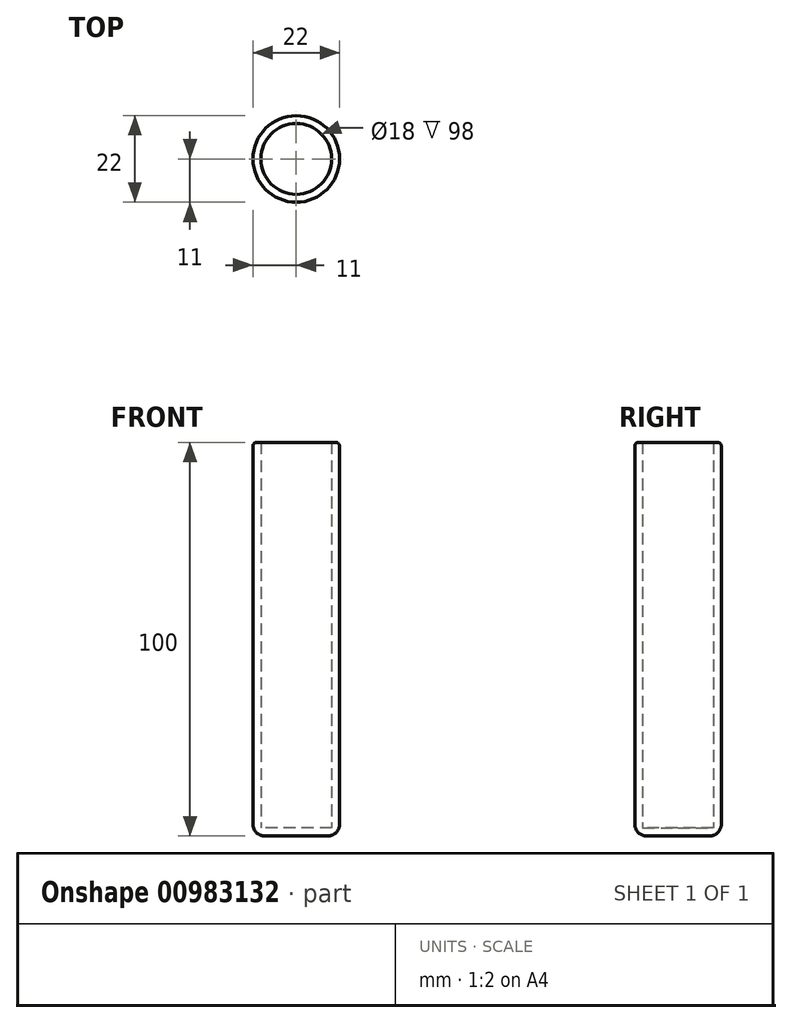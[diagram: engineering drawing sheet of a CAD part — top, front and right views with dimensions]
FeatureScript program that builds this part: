
annotation { "Feature Type Name" : "Feature", "Feature Type Description" : "" }
export const myFeature = defineFeature(function(context is Context, id is Id, definition is map)
    precondition{}
    {
        {
            var Q0;
            Q0=qCreatedBy(makeId("Top.planeOp"),FACE);
            var sketch = newSketch(context, id + "F0", { "sketchPlane" : qUnion([Q0])});
            skCircle(sketch, "E0", {"center": v(0, 0) * mm, "radius": 11 * mm});
            skSolve(sketch);
        }
        {
            var Q0;
            Q0=makeQuery(id+"F0.imprint","IMPRINT",FACE,{"disambiguationData":[TD([[makeQuery(id+"F0.imprint","IMPRINT",EDGE,{"derivedFrom":sQuery(id+"F0.wireOp",EDGE,"E0")}),1.0]])]});
            extrude(context, id + "F1", {"entities" : qUnion([Q0]), "depth" : 100 * mm, "offsetDistance" : 25 * mm});
        }
        {
            var Q0;
            Q0=makeQuery(id+"F1.opExtrude","CAP_FACE",FACE,{"disambiguationData":[OSD([sQuery(id+"F0.wireOp",EDGE,"E0")])],"isStart":false});
            shell(context, id + "F2", {"entities" : qUnion([Q0]), "thickness" : 2 * mm});
        }
        {
            var Q0;
            Q0=makeQuery(id+"F1.opExtrude","CAP_EDGE",EDGE,{"disambiguationData":[OSD([sQuery(id+"F0.wireOp",EDGE,"E0")])],"isStart":true});
            fillet(context, id + "F3", {"entities" : qUnion([Q0]), "radius" : 3 * mm, "tangentPropagation" : true, "allowEdgeOverflow" : false});
        }
        {
            var Q0;
            Q0=makeQuery(id+"F1.opExtrude","CAP_EDGE",EDGE,{"disambiguationData":[OSD([sQuery(id+"F0.wireOp",EDGE,"E0")])],"isStart":false});
            fillet(context, id + "F4", {"entities" : qUnion([Q0]), "radius" : 1 * mm, "tangentPropagation" : true, "allowEdgeOverflow" : false});
        }
    });
